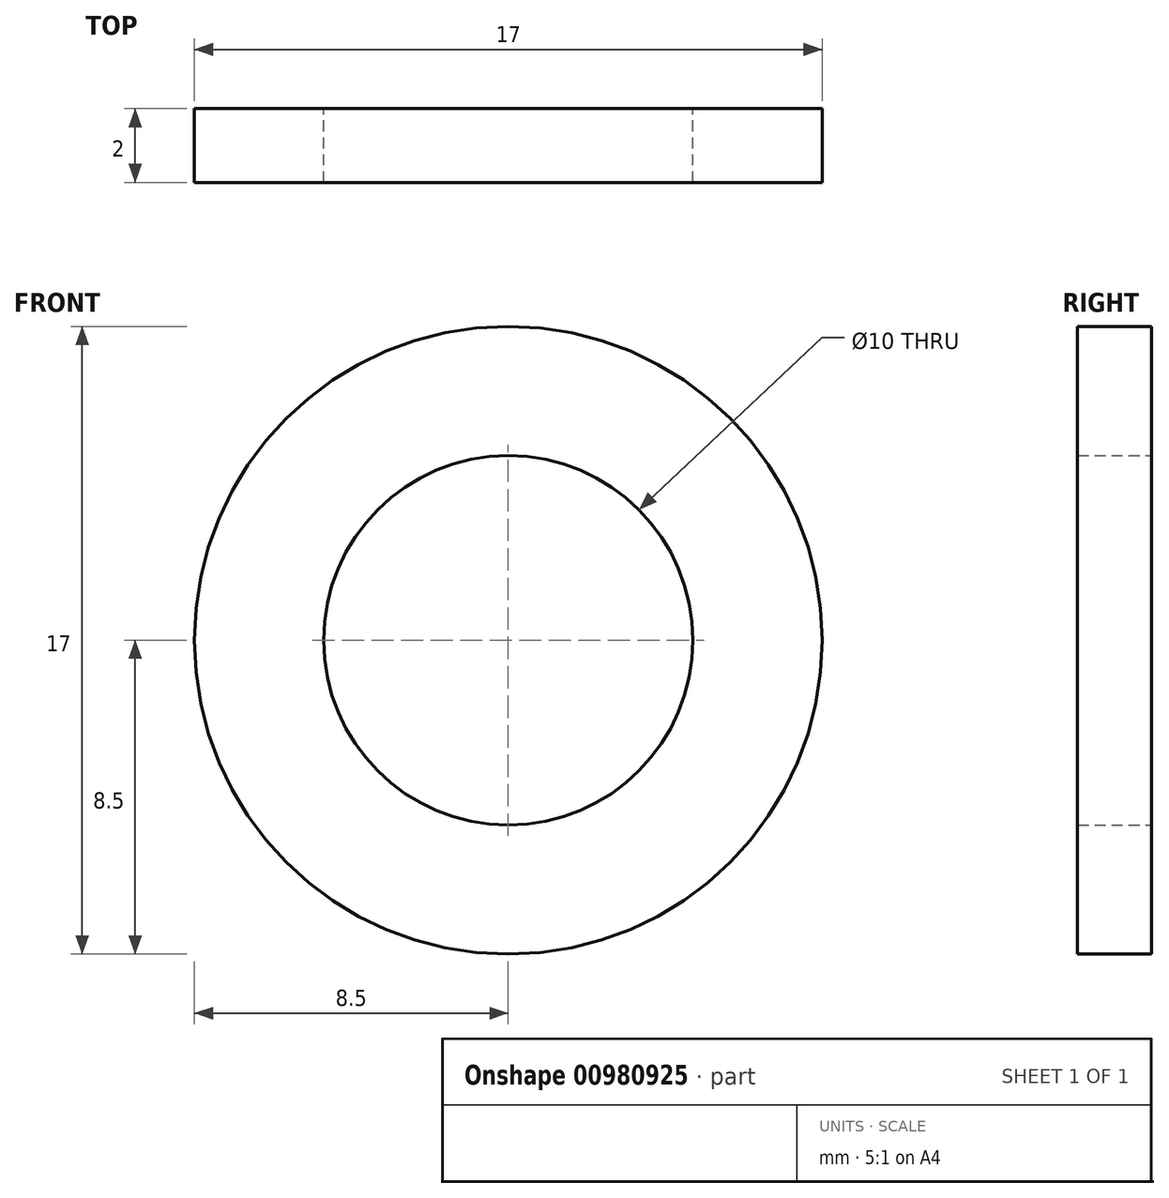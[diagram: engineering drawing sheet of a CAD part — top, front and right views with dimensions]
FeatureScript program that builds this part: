
annotation { "Feature Type Name" : "Feature", "Feature Type Description" : "" }
export const myFeature = defineFeature(function(context is Context, id is Id, definition is map)
    precondition{}
    {
        {
            var Q0;
            Q0=qCreatedBy(makeId("Front.planeOp"),FACE);
            var sketch = newSketch(context, id + "F0", { "sketchPlane" : qUnion([Q0])});
            skCircle(sketch, "E0", {"center": v(0, 0) * mm, "radius": 8.5 * mm});
            skCircle(sketch, "E1", {"center": v(0, 0) * mm, "radius": 5 * mm});
            skSolve(sketch);
        }
        {
            var Q0;
            Q0=makeQuery(id+"F0.imprint","IMPRINT",FACE,{"disambiguationData":[TD([[makeQuery(id+"F0.imprint","IMPRINT",EDGE,{"derivedFrom":sQuery(id+"F0.wireOp",EDGE,"E0")}),1.0]])]});
            extrude(context, id + "F1", {"entities" : qUnion([Q0]), "depth" : 2 * mm, "offsetDistance" : 25 * mm});
        }
    });
